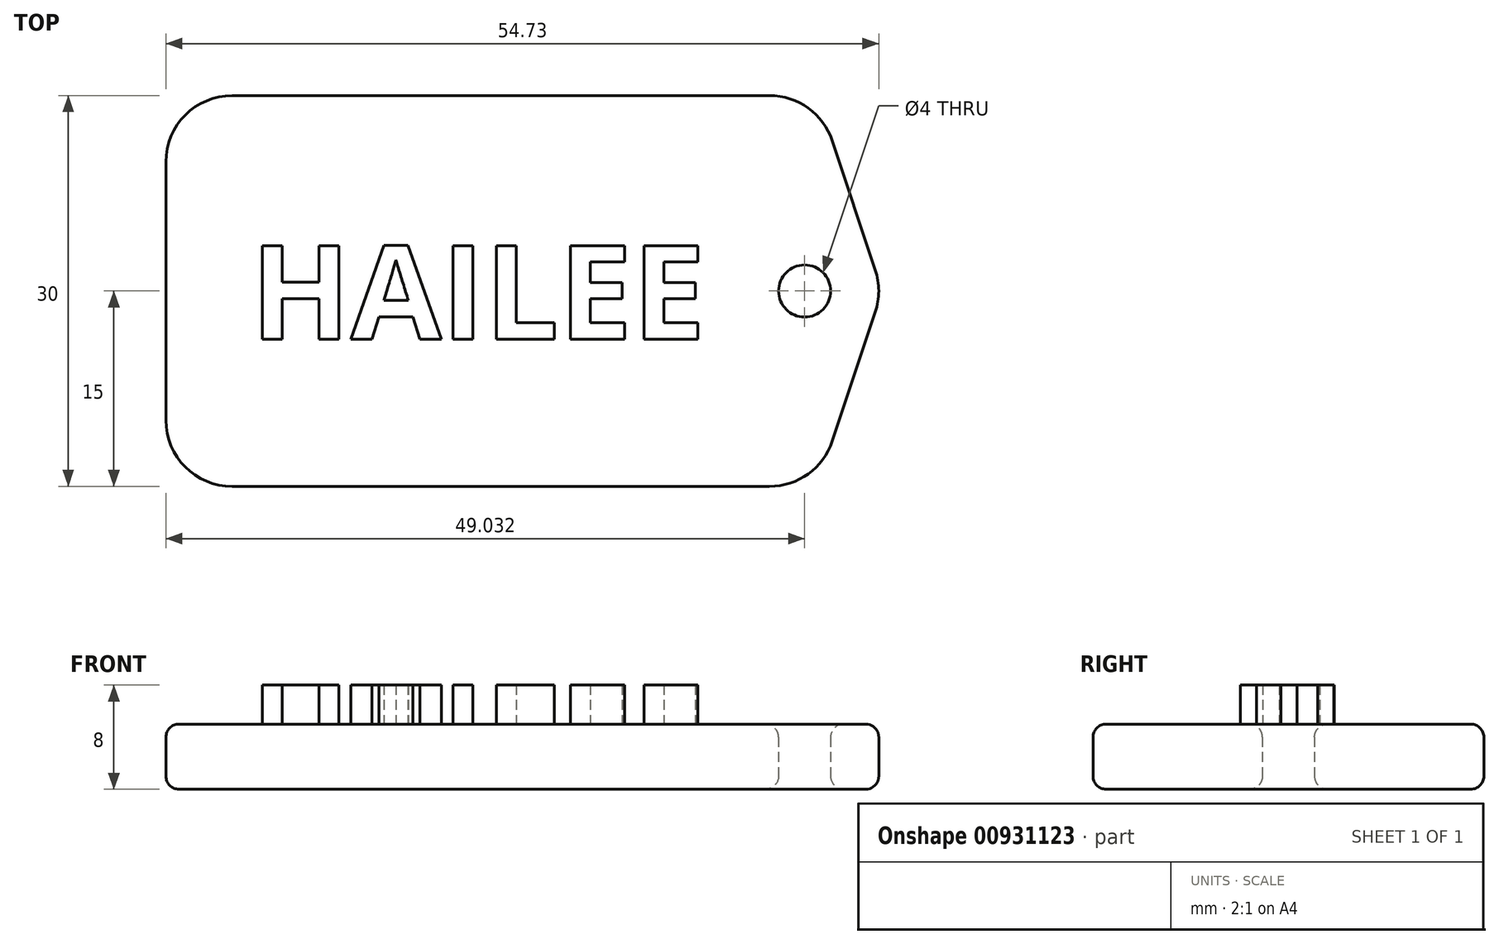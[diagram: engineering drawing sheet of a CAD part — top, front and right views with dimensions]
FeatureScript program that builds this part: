
annotation { "Feature Type Name" : "Feature", "Feature Type Description" : "" }
export const myFeature = defineFeature(function(context is Context, id is Id, definition is map)
    precondition{}
    {
        {
            var Q0;
            Q0=qCreatedBy(makeId("Top.planeOp"),FACE);
            var sketch = newSketch(context, id + "F0", { "sketchPlane" : qUnion([Q0])});
            skLineSegment(sketch, "E0.bottom", {"start": v(25, -15) * mm, "end": v(-25, -15) * mm});
            skLineSegment(sketch, "E0.top", {"start": v(25, 15) * mm, "end": v(-25, 15) * mm});
            skLineSegment(sketch, "E0.right", {"start": v(-25, -15) * mm, "end": v(-25, 15) * mm});
            skPoint(sketch, "E0.middle", {"position": v(0, 0) * mm});
            skPoint(sketch, "E1", {"position": v(30, 0) * mm});
            skLineSegment(sketch, "E2", {"start": v(25, 15) * mm, "end": v(30, 0) * mm});
            skLineSegment(sketch, "E3", {"start": v(25, -15) * mm, "end": v(30, 0) * mm});
            skSolve(sketch);
        }
        {
            var Q0;
            Q0=makeQuery(id+"F0.imprint","IMPRINT",FACE,{"disambiguationData":[TD([[makeQuery(id+"F0.imprint","IMPRINT",EDGE,{"derivedFrom":sQuery(id+"F0.wireOp",EDGE,"E0.bottom")}),-1.0]])]});
            extrude(context, id + "F1", {"entities" : qUnion([Q0]), "depth" : 5 * mm, "offsetDistance" : 25.4 * mm});
        }
        {
            var Q0;
            Q0=makeQuery(id+"F1.opExtrude","SWEPT_EDGE",EDGE,{"disambiguationData":[OSD([sQuery(id+"F0.wireOp",EDGE,"E2"),sQuery(id+"F0.wireOp",EDGE,"E3")])]});
            var Q1;
            Q1=makeQuery(id+"F1.opExtrude","SWEPT_EDGE",EDGE,{"disambiguationData":[OSD([sQuery(id+"F0.wireOp",EDGE,"E0.top"),sQuery(id+"F0.wireOp",EDGE,"E2")])]});
            var Q2;
            Q2=makeQuery(id+"F1.opExtrude","SWEPT_EDGE",EDGE,{"disambiguationData":[OSD([sQuery(id+"F0.wireOp",EDGE,"E0.bottom"),sQuery(id+"F0.wireOp",EDGE,"E3")])]});
            var Q3;
            Q3=makeQuery(id+"F1.opExtrude","SWEPT_EDGE",EDGE,{"disambiguationData":[OSD([sQuery(id+"F0.wireOp",EDGE,"E0.bottom"),sQuery(id+"F0.wireOp",EDGE,"E0.right")])]});
            var Q4;
            Q4=makeQuery(id+"F1.opExtrude","SWEPT_EDGE",EDGE,{"disambiguationData":[OSD([sQuery(id+"F0.wireOp",EDGE,"E0.top"),sQuery(id+"F0.wireOp",EDGE,"E0.right")])]});
            fillet(context, id + "F2", {"entities" : qUnion([Q0, Q1, Q2, Q3, Q4]), "radius" : 5.08 * mm, "tangentPropagation" : true, "allowEdgeOverflow" : false});
        }
        {
            var Q0;
            Q0=qCreatedBy(makeId("Top.planeOp"),FACE);
            var Q1;
            Q1=makeQuery(id+"F1.opExtrude","CAP_FACE",FACE,{"disambiguationData":[OSD([sQuery(id+"F0.wireOp",EDGE,"E0.bottom"),sQuery(id+"F0.wireOp",EDGE,"E0.top"),sQuery(id+"F0.wireOp",EDGE,"E0.right"),sQuery(id+"F0.wireOp",EDGE,"E2"),sQuery(id+"F0.wireOp",EDGE,"E3")])],"isStart":false});
            var sketch = newSketch(context, id + "F3", { "sketchPlane" : qUnion([Q0, Q1])});
            skPoint(sketch, "E4", {"position": v(24.03, 0) * mm});
            skSolve(sketch);
        }
        {
            var Q0;
            Q0=sQuery(id+"F3.wireOp",VERTEX,"E4");
            var Q1;
            Q1=makeQuery(id+"F1.opExtrude","SWEPT_BODY",BODY,{"disambiguationData":[OSD([sQuery(id+"F0.wireOp",EDGE,"E0.bottom"),sQuery(id+"F0.wireOp",EDGE,"E0.top"),sQuery(id+"F0.wireOp",EDGE,"E0.right"),sQuery(id+"F0.wireOp",EDGE,"E2"),sQuery(id+"F0.wireOp",EDGE,"E3")])]});
            hole(context, id + "F4", {"style" : HoleStyle.SIMPLE, "endStyle" : HoleEndStyle.THROUGH, "oppositeDirection" : true, "holeDiameter" : 4 * mm, "majorDiameter" : 6.35 * mm, "isTappedThrough" : true, "tappedDepth" : 12.7 * mm, "tapClearance" : 3, "locations" : qUnion([Q0]), "scope" : qUnion([Q1])});
        }
        {
            var Q0;
            Q0=makeQuery(id+"F1.opExtrude","CAP_FACE",FACE,{"disambiguationData":[OSD([sQuery(id+"F0.wireOp",EDGE,"E0.bottom"),sQuery(id+"F0.wireOp",EDGE,"E0.top"),sQuery(id+"F0.wireOp",EDGE,"E0.right"),sQuery(id+"F0.wireOp",EDGE,"E2"),sQuery(id+"F0.wireOp",EDGE,"E3")])],"isStart":false});
            var Q1;
            Q1=makeQuery(id+"F1.opExtrude","CAP_FACE",FACE,{"disambiguationData":[OSD([sQuery(id+"F0.wireOp",EDGE,"E0.bottom"),sQuery(id+"F0.wireOp",EDGE,"E0.top"),sQuery(id+"F0.wireOp",EDGE,"E0.right"),sQuery(id+"F0.wireOp",EDGE,"E2"),sQuery(id+"F0.wireOp",EDGE,"E3")])],"isStart":true});
            fillet(context, id + "F5", {"entities" : qUnion([Q0, Q1]), "radius" : 1 * mm, "tangentPropagation" : true, "allowEdgeOverflow" : false});
        }
        {
            var Q0;
            Q0=makeQuery(id+"F1.opExtrude","CAP_FACE",FACE,{"disambiguationData":[OSD([sQuery(id+"F0.wireOp",EDGE,"E0.bottom"),sQuery(id+"F0.wireOp",EDGE,"E0.top"),sQuery(id+"F0.wireOp",EDGE,"E0.right"),sQuery(id+"F0.wireOp",EDGE,"E2"),sQuery(id+"F0.wireOp",EDGE,"E3")])],"isStart":false});
            var sketch = newSketch(context, id + "F6", { "sketchPlane" : qUnion([Q0])});
            skText(sketch, "E5", { "text": "HAILEE", "fontName": "OpenSans-Bold.ttf"});
            const initialGuessF6  = {"E5": [-0.01852, -0.0037, 1, 0, 0.00725]};
            skSetInitialGuess(sketch, initialGuessF6);
            skSolve(sketch);
        }
        {
            var Q0;
            Q0 = qSketchRegion(id + "F6", true);
            extrude(context, id + "F7", {"entities" : qUnion([Q0]), "operationType" : NewBodyOperationType.ADD, "depth" : 3 * mm, "offsetDistance" : 25.4 * mm});
        }
    });
